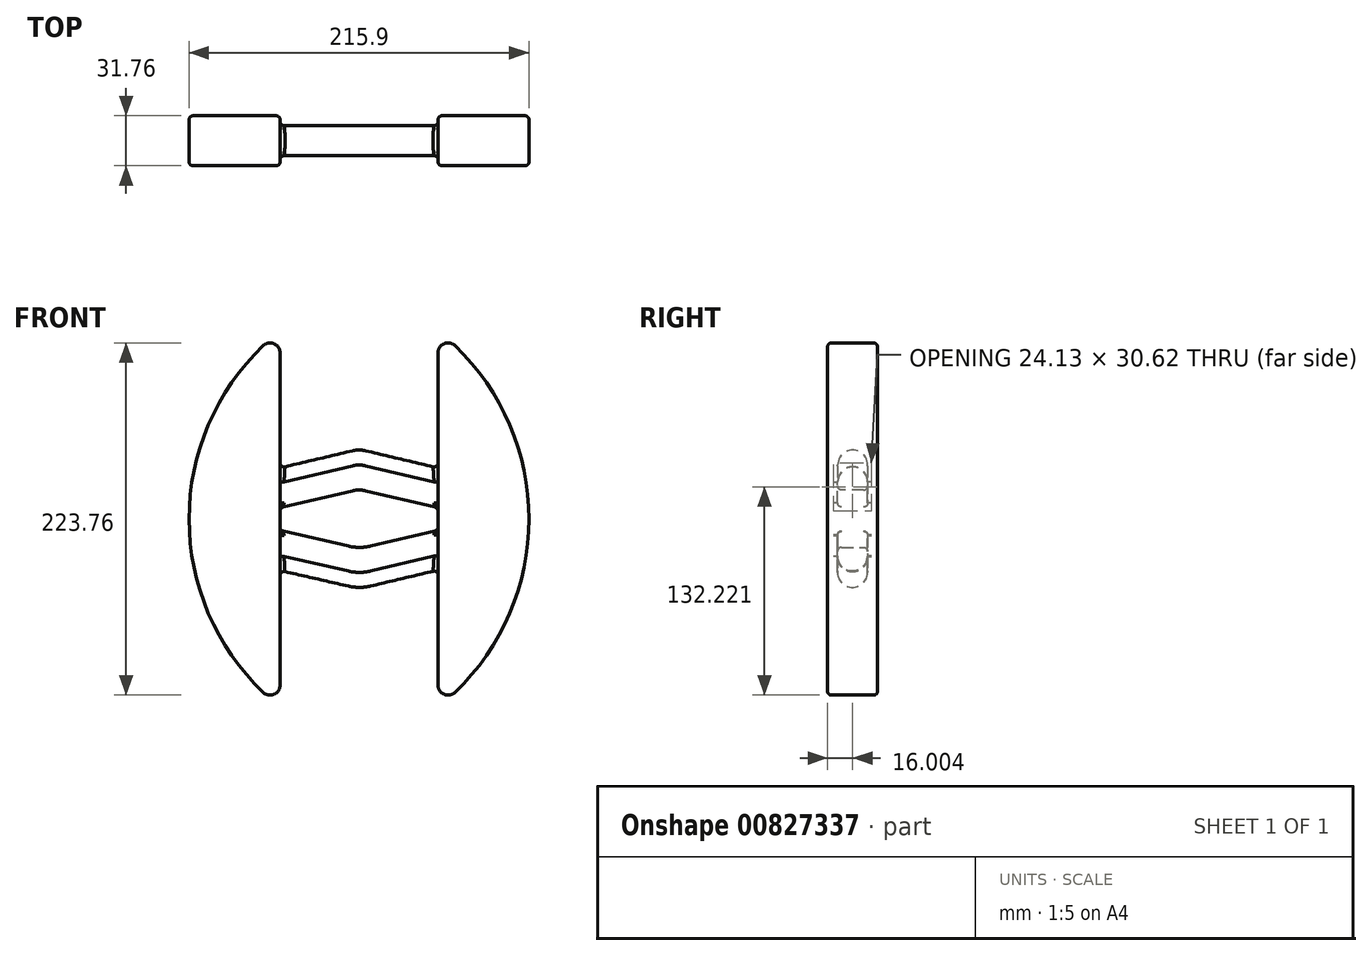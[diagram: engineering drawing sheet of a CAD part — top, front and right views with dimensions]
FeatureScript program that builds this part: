
annotation { "Feature Type Name" : "Feature", "Feature Type Description" : "" }
export const myFeature = defineFeature(function(context is Context, id is Id, definition is map)
    precondition{}
    {
        {
            var Q0;
            Q0=qCreatedBy(makeId("Front.planeOp"),FACE);
            var sketch = newSketch(context, id + "F0", { "sketchPlane" : qUnion([Q0])});
            skLineSegment(sketch, "E0.0", {"start": v(-50.17, 7.04) * mm, "end": v(-4.25, 17.93) * mm});
            skArc(sketch, "E1.0", {"start": v(4.25, 17.93) * mm, "mid": v(0, 18.43) * mm, "end": v(-4.25, 17.93) * mm});
            skLineSegment(sketch, "E2.0", {"start": v(4.25, 17.93) * mm, "end": v(50.16, 7.04) * mm});
            skLineSegment(sketch, "E3.0", {"start": v(4.48, -17.85) * mm, "end": v(50.16, -7.02) * mm});
            skArc(sketch, "E4.0", {"start": v(-3.97, -17.86) * mm, "mid": v(0.25, -18.35) * mm, "end": v(4.48, -17.85) * mm});
            skLineSegment(sketch, "E5.0", {"start": v(-50.17, -7.04) * mm, "end": v(-3.97, -17.86) * mm});
            skLineSegment(sketch, "E6.0", {"start": v(-50.17, 20.1) * mm, "end": v(-7.18, 30.29) * mm});
            skArc(sketch, "E7.0", {"start": v(7.18, 30.29) * mm, "mid": v(0, 31.13) * mm, "end": v(-7.18, 30.29) * mm});
            skArc(sketch, "E8.0", {"start": v(-6.7, -30.27) * mm, "mid": v(0.35, -31.05) * mm, "end": v(7.4, -30.2) * mm});
            skLineSegment(sketch, "E9.0", {"start": v(7.4, -30.2) * mm, "end": v(50.16, -20.07) * mm});
            skLineSegment(sketch, "E10", {"start": v(-50.17, -20.33) * mm, "end": v(-6.7, -30.27) * mm});
            skLineSegment(sketch, "E11", {"start": v(7.18, 30.29) * mm, "end": v(50.16, 20.1) * mm});
            skLineSegment(sketch, "E12", {"start": v(-50.17, 20.1) * mm, "end": v(-50.17, 7.04) * mm});
            skLineSegment(sketch, "E13", {"start": v(50.16, 20.1) * mm, "end": v(50.16, 7.04) * mm});
            skLineSegment(sketch, "E14.trimOffspring", {"start": v(-50.17, -7.04) * mm, "end": v(-50.17, -20.33) * mm});
            skLineSegment(sketch, "E15.trimOffspring", {"start": v(50.16, -7.02) * mm, "end": v(50.16, -20.07) * mm});
            skSolve(sketch);
        }
        {
            var Q0;
            Q0=sQuery(id+"F0.wireOp",VERTEX,"E11.end");
            var Q1;
            Q1=qCreatedBy(makeId("Right.planeOp"),FACE);
            cPlane(context, id + "F1", {"entities" : qUnion([Q0, Q1]), "cplaneType" : CPlaneType.PLANE_POINT, "offset" : 25.4 * mm, "width" : 152.4 * mm, "height" : 152.4 * mm});
        }
        {
            var Q0;
            Q0=qCreatedBy(id+"F1.planeOp",FACE);
            var sketch = newSketch(context, id + "F2", { "sketchPlane" : qUnion([Q0])});
            skLineSegment(sketch, "E16.top", {"start": v(-9.4, 7.04) * mm, "end": v(9.65, 7.04) * mm});
            skLineSegment(sketch, "E16.left", {"start": v(-9.4, 22.91) * mm, "end": v(-9.4, 7.04) * mm});
            skLineSegment(sketch, "E16.right", {"start": v(9.65, 22.91) * mm, "end": v(9.65, 7.04) * mm});
            skArc(sketch, "E17", {"start": v(9.65, 22.91) * mm, "mid": v(0.12, 32.44) * mm, "end": v(-9.4, 22.91) * mm});
            skPoint(sketch, "E17.third.point", {"position": v(0, 32.44) * mm});
            skSolve(sketch);
        }
        {
            var Q0;
            Q0=makeQuery(id+"F2.imprint","IMPRINT",FACE,{"disambiguationData":[TD([[makeQuery(id+"F2.imprint","IMPRINT",EDGE,{"derivedFrom":sQuery(id+"F2.wireOp",EDGE,"E16.top")}),1.0]])]});
            var Q1;
            Q1=sQuery(id+"F0.wireOp",EDGE,"E2.0");
            var Q2;
            Q2=sQuery(id+"F0.wireOp",EDGE,"E1.0");
            var Q3;
            Q3=sQuery(id+"F0.wireOp",EDGE,"E0.0");
            sweep(context, id + "F3", {"profiles" : qUnion([Q0]), "path" : qUnion([Q1, Q2, Q3]), "keepProfileOrientation" : true});
        }
        {
            var Q0;
            Q0=qCreatedBy(id+"F1.planeOp",FACE);
            var sketch = newSketch(context, id + "F4", { "sketchPlane" : qUnion([Q0])});
            skLineSegment(sketch, "E18.bottom", {"start": v(-9.52, -7.04) * mm, "end": v(9.53, -7.04) * mm});
            skLineSegment(sketch, "E18.left", {"start": v(-9.52, -7.04) * mm, "end": v(-9.53, -22.91) * mm});
            skLineSegment(sketch, "E18.right", {"start": v(9.53, -7.04) * mm, "end": v(9.52, -22.91) * mm});
            skArc(sketch, "E19", {"start": v(-9.53, -22.91) * mm, "mid": v(0, -32.44) * mm, "end": v(9.53, -22.91) * mm});
            skPoint(sketch, "E19.third.point", {"position": v(0, -32.44) * mm});
            skSolve(sketch);
        }
        {
            var Q0;
            Q0=makeQuery(id+"F4.imprint","IMPRINT",FACE,{"disambiguationData":[TD([[makeQuery(id+"F4.imprint","IMPRINT",EDGE,{"derivedFrom":sQuery(id+"F4.wireOp",EDGE,"E18.bottom")}),-1.0]])]});
            var Q1;
            Q1=sQuery(id+"F0.wireOp",EDGE,"E9.0");
            var Q2;
            Q2=sQuery(id+"F0.wireOp",EDGE,"E8.0");
            var Q3;
            Q3=sQuery(id+"F0.wireOp",EDGE,"E10");
            sweep(context, id + "F5", {"profiles" : qUnion([Q0]), "path" : qUnion([Q1, Q2, Q3]), "keepProfileOrientation" : true});
        }
        {
            var Q0;
            Q0=qCreatedBy(makeId("Front.planeOp"),FACE);
            var sketch = newSketch(context, id + "F6", { "sketchPlane" : qUnion([Q0])});
            skLineSegment(sketch, "E20", {"start": v(-50.17, 105.53) * mm, "end": v(-50.17, -105.53) * mm});
            skArc(sketch, "E21", {"start": v(-60.9, 110.12) * mm, "mid": v(-107.95, 0) * mm, "end": v(-60.9, -110.12) * mm});
            skPoint(sketch, "E22.visualSharp", {"position": v(-50.17, 119.47) * mm});
            skArc(sketch, "E22.filletArc", {"start": v(-50.17, 105.53) * mm, "mid": v(-54.02, 111.37) * mm, "end": v(-60.9, 110.12) * mm});
            skPoint(sketch, "E23.visualSharp", {"position": v(-50.17, -119.47) * mm});
            skArc(sketch, "E23.filletArc", {"start": v(-60.9, -110.12) * mm, "mid": v(-54.02, -111.37) * mm, "end": v(-50.17, -105.53) * mm});
            skLineSegment(sketch, "E24", {"start": v(50.16, 105.53) * mm, "end": v(50.16, -105.53) * mm});
            skArc(sketch, "E25", {"start": v(60.9, -110.12) * mm, "mid": v(107.95, 0) * mm, "end": v(60.9, 110.12) * mm});
            skPoint(sketch, "E26.visualSharp", {"position": v(50.16, 119.48) * mm});
            skArc(sketch, "E26.filletArc", {"start": v(60.9, 110.12) * mm, "mid": v(54.02, 111.37) * mm, "end": v(50.16, 105.53) * mm});
            skPoint(sketch, "E27.visualSharp", {"position": v(50.16, -119.48) * mm});
            skArc(sketch, "E27.filletArc", {"start": v(50.16, -105.53) * mm, "mid": v(54.02, -111.37) * mm, "end": v(60.9, -110.12) * mm});
            skSolve(sketch);
        }
        {
            var Q0;
            Q0 = qSketchRegion(id + "F6", true);
            extrude(context, id + "F7", {"entities" : qUnion([Q0]), "operationType" : NewBodyOperationType.ADD, "depth" : 31.75 * mm, "offsetDistance" : 25.4 * mm, "symmetric" : true});
        }
        {
            var Q0;
            Q0=makeQuery(id+"F7.opExtrude","CAP_FACE",FACE,{"disambiguationData":[OSD([sQuery(id+"F6.wireOp",EDGE,"E20"),sQuery(id+"F6.wireOp",EDGE,"E21"),sQuery(id+"F6.wireOp",EDGE,"E22.filletArc"),sQuery(id+"F6.wireOp",EDGE,"E23.filletArc")])],"isStart":false});
            var Q1;
            Q1=makeQuery(id+"F7.opExtrude","CAP_FACE",FACE,{"disambiguationData":[OSD([sQuery(id+"F6.wireOp",EDGE,"E24"),sQuery(id+"F6.wireOp",EDGE,"E25"),sQuery(id+"F6.wireOp",EDGE,"E26.filletArc"),sQuery(id+"F6.wireOp",EDGE,"E27.filletArc")])],"isStart":false});
            var Q2;
            Q2=makeQuery(id+"F7.opExtrude","CAP_FACE",FACE,{"disambiguationData":[OSD([sQuery(id+"F6.wireOp",EDGE,"E20"),sQuery(id+"F6.wireOp",EDGE,"E21"),sQuery(id+"F6.wireOp",EDGE,"E22.filletArc"),sQuery(id+"F6.wireOp",EDGE,"E23.filletArc")])],"isStart":true});
            var Q3;
            Q3=makeQuery(id+"F7.opExtrude","CAP_FACE",FACE,{"disambiguationData":[OSD([sQuery(id+"F6.wireOp",EDGE,"E24"),sQuery(id+"F6.wireOp",EDGE,"E25"),sQuery(id+"F6.wireOp",EDGE,"E26.filletArc"),sQuery(id+"F6.wireOp",EDGE,"E27.filletArc")])],"isStart":true});
            var Q4;
            Q4=makeQuery(id+"F7.opExtrude","SWEPT_FACE",FACE,{"disambiguationData":[OSD([sQuery(id+"F6.wireOp",EDGE,"E20")])]});
            var Q5;
            Q5=makeQuery(id+"F7.opExtrude","SWEPT_FACE",FACE,{"disambiguationData":[OSD([sQuery(id+"F6.wireOp",EDGE,"E24")])]});
            var Q6;
            Q6=makeQuery(id+"F5.opSweep","SWEPT_FACE",FACE,{"disambiguationData":[OSD([sQuery(id+"F0.wireOp",EDGE,"E9.0"),sQuery(id+"F4.wireOp",EDGE,"E18.left")])]});
            var Q7;
            Q7=makeQuery(id+"F3.opSweep","SWEPT_FACE",FACE,{"disambiguationData":[OSD([sQuery(id+"F0.wireOp",EDGE,"E2.0"),sQuery(id+"F2.wireOp",EDGE,"E16.left")])]});
            var Q8;
            Q8=makeQuery(id+"F5.opSweep","SWEPT_FACE",FACE,{"disambiguationData":[OSD([sQuery(id+"F0.wireOp",EDGE,"E9.0"),sQuery(id+"F4.wireOp",EDGE,"E18.right")])]});
            var Q9;
            Q9=makeQuery(id+"F3.opSweep","SWEPT_FACE",FACE,{"disambiguationData":[OSD([sQuery(id+"F0.wireOp",EDGE,"E2.0"),sQuery(id+"F2.wireOp",EDGE,"E16.right")])]});
            fillet(context, id + "F8", {"entities" : qUnion([Q0, Q1, Q2, Q3, Q4, Q5, Q6, Q7, Q8, Q9]), "radius" : 2.54 * mm, "tangentPropagation" : true, "allowEdgeOverflow" : false});
        }
    });
